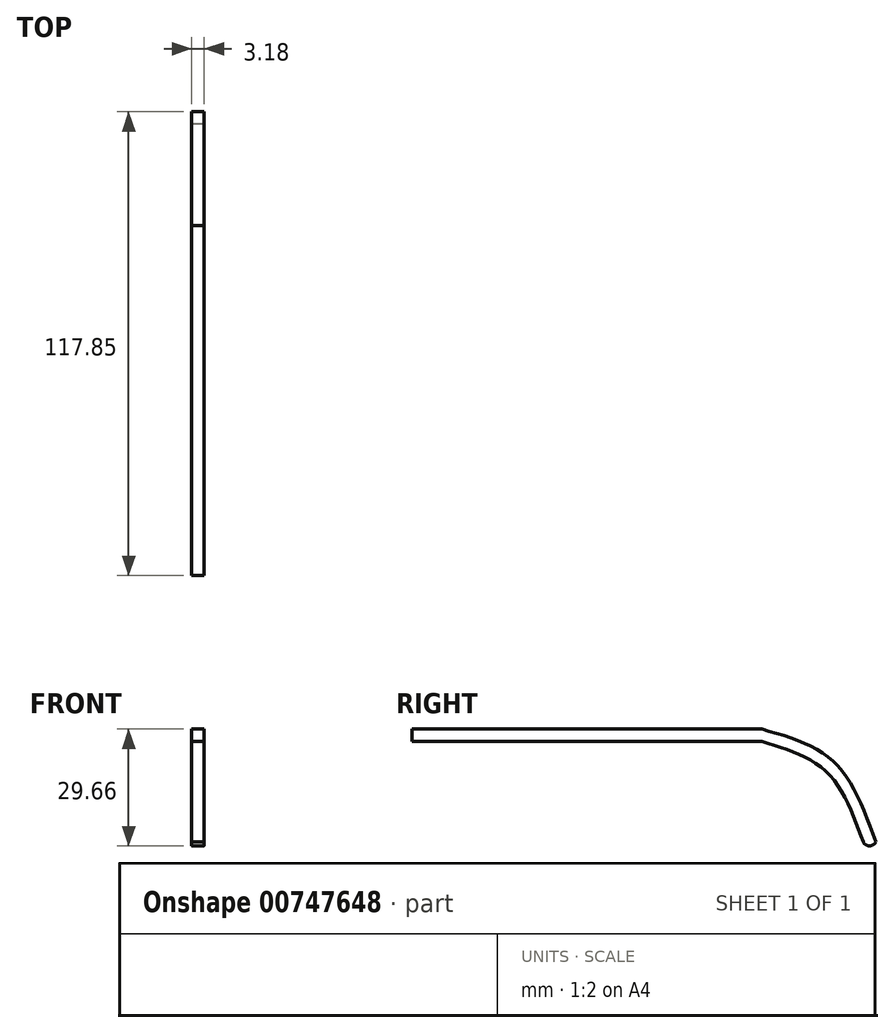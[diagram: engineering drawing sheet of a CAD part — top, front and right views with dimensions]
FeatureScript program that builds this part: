
annotation { "Feature Type Name" : "Feature", "Feature Type Description" : "" }
export const myFeature = defineFeature(function(context is Context, id is Id, definition is map)
    precondition{}
    {
        {
            var Q0;
            Q0=qCreatedBy(makeId("Right.planeOp"),FACE);
            var sketch = newSketch(context, id + "F0", { "sketchPlane" : qUnion([Q0])});
            skLineSegment(sketch, "E0", {"start": v(-59, 9.95) * mm, "end": v(29.9, 9.95) * mm});
            skLineSegment(sketch, "E1", {"start": v(-59, 9.95) * mm, "end": v(-59, 6.78) * mm});
            skLineSegment(sketch, "E2", {"start": v(-59, 6.78) * mm, "end": v(29.9, 6.78) * mm});
            skFitSpline(sketch, "E3", {"points": [v(29.9, 9.95) * mm, v(48.18, 1.66) * mm, v(58.86, -18.77) * mm], "startDerivative": vector(43.52, -12.46) * mm, "endDerivative": vector(17.42, -48.08) * mm});
            skFitSpline(sketch, "E4", {"points": [v(29.9, 6.78) * mm, v(46.36, -0.94) * mm, v(55.69, -18.77) * mm], "startDerivative": vector(36.26, -11.1) * mm, "endDerivative": vector(13.41, -36.8) * mm});
            skArc(sketch, "E5", {"start": v(55.69, -18.77) * mm, "mid": v(57.27, -19.7) * mm, "end": v(58.86, -18.77) * mm});
            skSolve(sketch);
        }
        {
            var Q0;
            Q0=makeQuery(id+"F0.imprint","IMPRINT",FACE,{"disambiguationData":[TD([[makeQuery(id+"F0.imprint","IMPRINT",EDGE,{"derivedFrom":sQuery(id+"F0.wireOp",EDGE,"E0")}),-1.0]])]});
            extrude(context, id + "F1", {"entities" : qUnion([Q0]), "depth" : 3.17 * mm, "offsetDistance" : 25.4 * mm});
        }
    });
